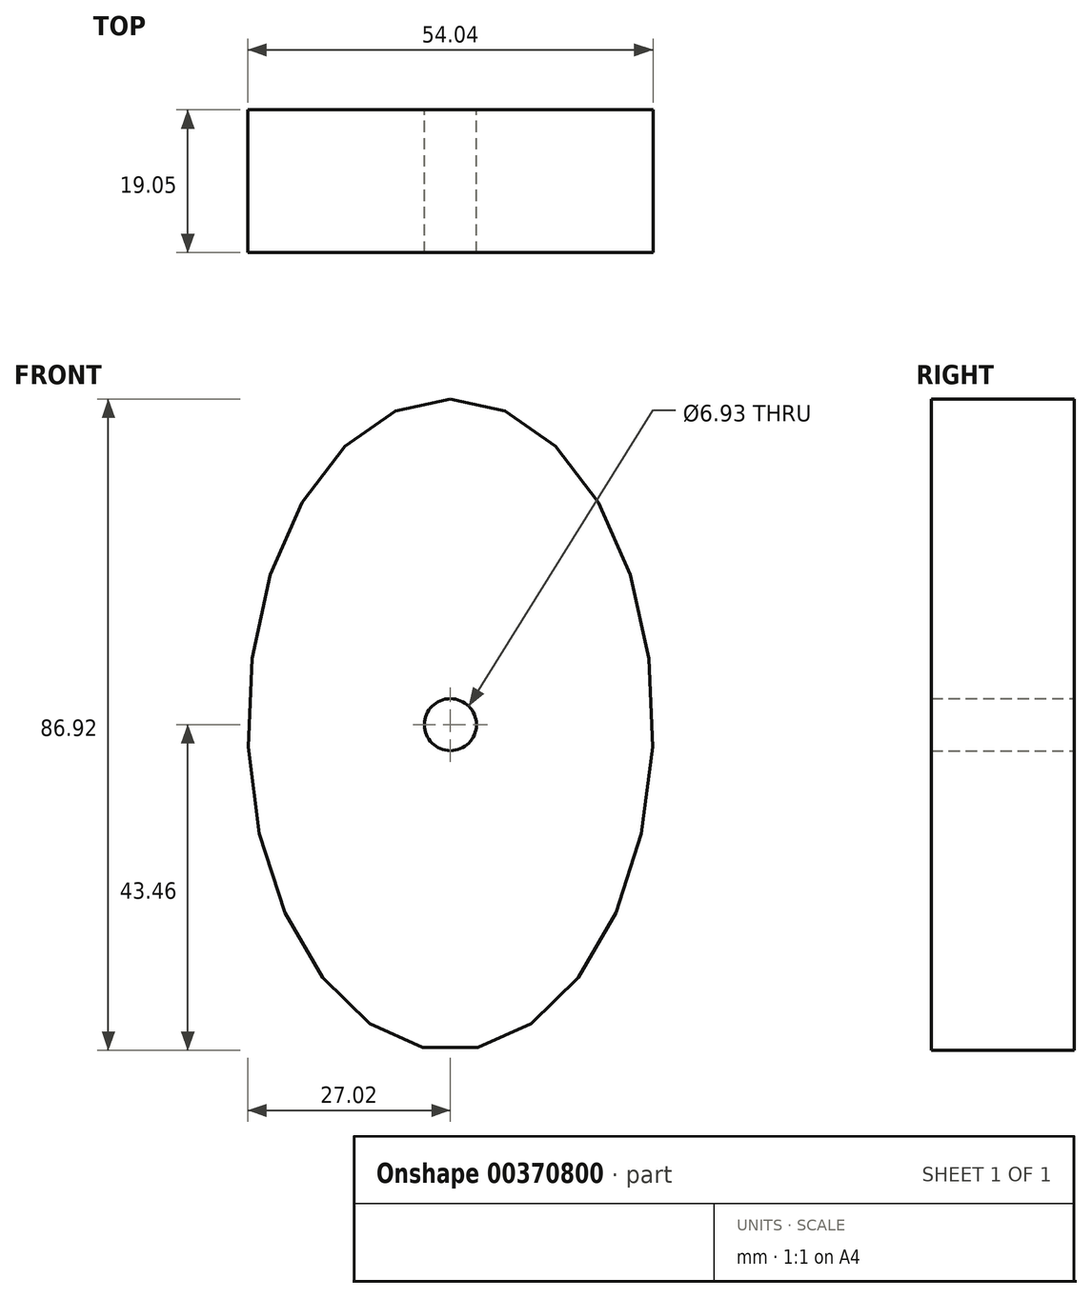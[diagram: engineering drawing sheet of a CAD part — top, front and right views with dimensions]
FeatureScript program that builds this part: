
annotation { "Feature Type Name" : "Feature", "Feature Type Description" : "" }
export const myFeature = defineFeature(function(context is Context, id is Id, definition is map)
    precondition{}
    {
        {
            var Q0;
            Q0=qCreatedBy(makeId("Front.planeOp"),FACE);
            var sketch = newSketch(context, id + "F0", { "sketchPlane" : qUnion([Q0])});
            skEllipse(sketch, "E0", {"center": v(0, 0) * mm, "majorRadius": 43.46 * mm, "minorRadius": 27.02 * mm, "majorAxis": v(0, 1)});
            skSolve(sketch);
        }
        {
            var Q0;
            Q0 = qSketchRegion(id + "F0", true);
            extrude(context, id + "F1", {"entities" : qUnion([Q0]), "depth" : 19.05 * mm});
        }
        {
            var Q0;
            Q0=qCreatedBy(makeId("Front.planeOp"),FACE);
            var sketch = newSketch(context, id + "F2", { "sketchPlane" : qUnion([Q0])});
            skCircle(sketch, "E1", {"center": v(0, 0) * mm, "radius": 3.47 * mm});
            skSolve(sketch);
        }
        {
            var Q0;
            Q0 = qSketchRegion(id + "F2", true);
            extrude(context, id + "F3", {"entities" : qUnion([Q0]), "operationType" : NewBodyOperationType.REMOVE, "depth" : 25.4 * mm});
        }
    });
